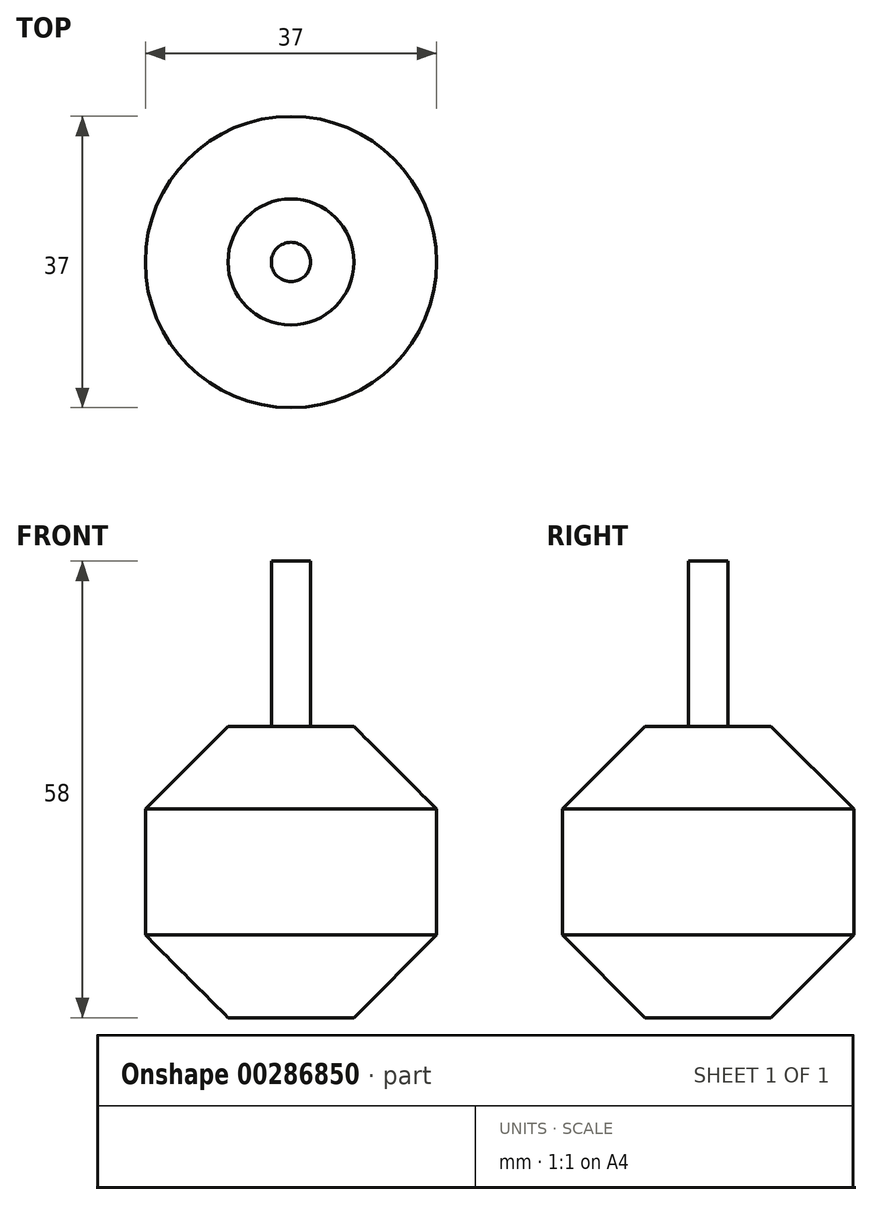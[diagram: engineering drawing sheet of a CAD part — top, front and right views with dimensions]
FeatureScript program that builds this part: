
annotation { "Feature Type Name" : "Feature", "Feature Type Description" : "" }
export const myFeature = defineFeature(function(context is Context, id is Id, definition is map)
    precondition{}
    {
        {
            var Q0;
            Q0=qCreatedBy(makeId("Top.planeOp"),FACE);
            var sketch = newSketch(context, id + "F0", { "sketchPlane" : qUnion([Q0])});
            skCircle(sketch, "E0", {"center": v(-45.23, 10.87) * mm, "radius": 18.5 * mm});
            skSolve(sketch);
        }
        {
            var Q0;
            Q0 = qSketchRegion(id + "F0", true);
            extrude(context, id + "F1", {"entities" : qUnion([Q0]), "depth" : 16 * mm});
        }
        {
            var Q0;
            Q0=makeQuery(id+"F1.opExtrude","CAP_FACE",FACE,{"disambiguationData":[OSD([sQuery(id+"F0.wireOp",EDGE,"E0")])],"isStart":true});
            var sketch = newSketch(context, id + "F2", { "sketchPlane" : qUnion([Q0])});
            skCircle(sketch, "E1", {"center": v(-45.23, -10.87) * mm, "radius": 18.5 * mm});
            skSolve(sketch);
        }
        {
            var Q0;
            Q0 = qSketchRegion(id + "F2", true);
            extrude(context, id + "F3", {"entities" : qUnion([Q0]), "operationType" : NewBodyOperationType.ADD, "depth" : 10.5 * mm});
        }
        {
            var Q0;
            Q0=makeQuery(id+"F3.opExtrude","CAP_FACE",FACE,{"disambiguationData":[OSD([sQuery(id+"F2.wireOp",EDGE,"E1")])],"isStart":false});
            chamfer(context, id + "F4", {"entities" : qUnion([Q0]), "chamferType" : ChamferType.OFFSET_ANGLE, "width" : 10.5 * mm, "oppositeDirection" : false, "angle" : 45 * degree, "tangentPropagation" : true});
        }
        {
            var Q0;
            Q0=makeQuery(id+"F1.opExtrude","CAP_FACE",FACE,{"disambiguationData":[OSD([sQuery(id+"F0.wireOp",EDGE,"E0")])],"isStart":false});
            var sketch = newSketch(context, id + "F5", { "sketchPlane" : qUnion([Q0])});
            skCircle(sketch, "E2", {"center": v(-45.23, 10.87) * mm, "radius": 18.5 * mm});
            skSolve(sketch);
        }
        {
            var Q0;
            Q0 = qSketchRegion(id + "F5", true);
            extrude(context, id + "F6", {"entities" : qUnion([Q0]), "operationType" : NewBodyOperationType.ADD, "depth" : 10.5 * mm});
        }
        {
            var Q0;
            Q0=makeQuery(id+"F6.opExtrude","CAP_FACE",FACE,{"disambiguationData":[OSD([sQuery(id+"F5.wireOp",EDGE,"E2")])],"isStart":false});
            chamfer(context, id + "F7", {"entities" : qUnion([Q0]), "chamferType" : ChamferType.OFFSET_ANGLE, "width" : 10.5 * mm, "oppositeDirection" : false, "angle" : 45 * degree, "tangentPropagation" : true});
        }
        {
            var Q0;
            Q0=makeQuery(id+"F6.opExtrude","CAP_FACE",FACE,{"disambiguationData":[OSD([sQuery(id+"F5.wireOp",EDGE,"E2")])],"isStart":false});
            var sketch = newSketch(context, id + "F8", { "sketchPlane" : qUnion([Q0])});
            skCircle(sketch, "E3", {"center": v(-45.23, 10.87) * mm, "radius": 2.5 * mm});
            skSolve(sketch);
        }
        {
            var Q0;
            Q0 = qSketchRegion(id + "F8", true);
            extrude(context, id + "F9", {"entities" : qUnion([Q0]), "operationType" : NewBodyOperationType.ADD, "depth" : 21 * mm});
        }
    });
